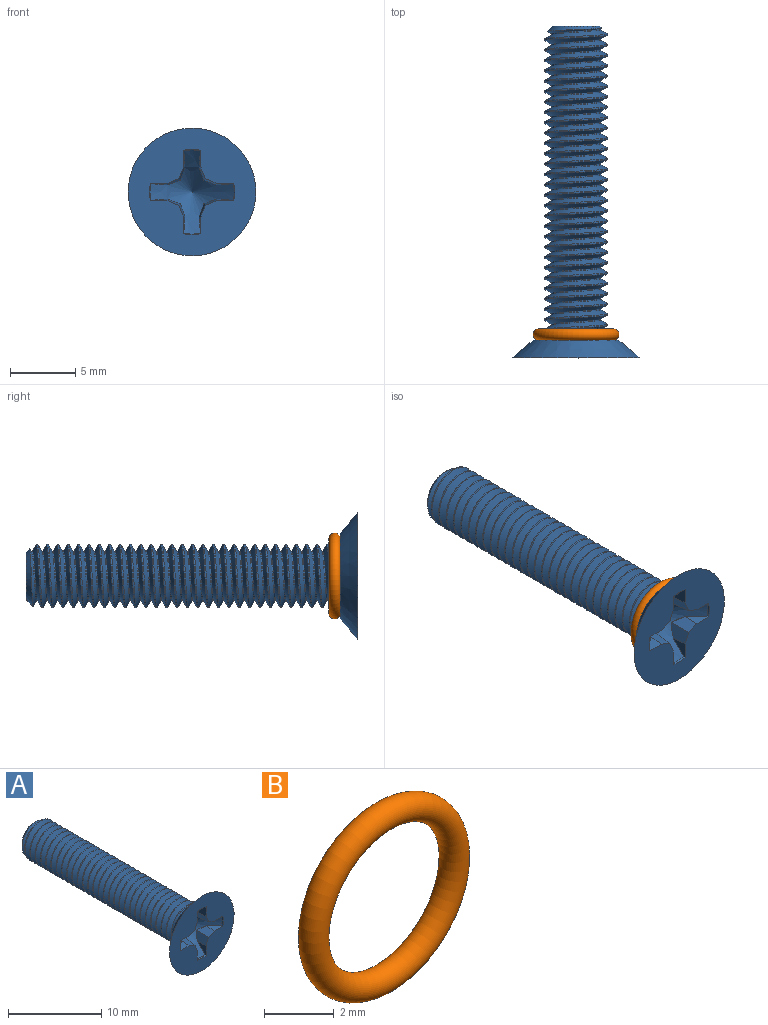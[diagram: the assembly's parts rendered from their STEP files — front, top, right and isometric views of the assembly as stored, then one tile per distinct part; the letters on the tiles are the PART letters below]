
ASSEMBLY  parts=2 mates=1
PART A: 60 faces, bbox 10.1x26x10.1 mm
  f0: cone r=4.27mm half-angle=50deg, axis (0,-1,0), area 20.8mm2, adj f1,f41,f42,f43,f44,f45,f46,f47
  f1: cone r=3.26mm half-angle=15deg, axis (0,-1,0), area 0.2mm2, adj f0,f40,f45,f56
  f2: cone r=4.89mm half-angle=50deg, axis (0,-1,0), area 53.8mm2, adj f39,f40
  f3: cylinder r=1.88mm len=23.12mm, axis (0,-1,0), area 34.1mm2, adj f33,f36,f37,f38
  f4: cylinder r=2.41mm len=4.83mm, axis (0,-1,0), area 14.2mm2, adj f5,f36,f37,f38,f39
  f5: cylinder r=2.41mm len=4.83mm, axis (0,-1,0), area 1.5mm2, adj f4,f6,f36,f37
  f6: cylinder r=2.41mm len=4.83mm, axis (0,-1,0), area 1.5mm2, adj f5,f7,f36,f37
  f7: cylinder r=2.41mm len=4.83mm, axis (0,-1,0), area 1.5mm2, adj f6,f8,f36,f37
  f8: cylinder r=2.41mm len=4.83mm, axis (0,-1,0), area 1.5mm2, adj f7,f9,f36,f37
  f9: cylinder r=2.41mm len=4.83mm, axis (0,-1,0), area 1.5mm2, adj f8,f10,f36,f37
  f10: cylinder r=2.41mm len=4.83mm, axis (0,-1,0), area 1.5mm2, adj f9,f11,f36,f37
  f11: cylinder r=2.41mm len=4.83mm, axis (0,-1,0), area 1.5mm2, adj f10,f12,f36,f37
  f12: cylinder r=2.41mm len=4.83mm, axis (0,-1,0), area 1.5mm2, adj f11,f13,f36,f37
  f13: cylinder r=2.41mm len=4.83mm, axis (0,-1,0), area 1.5mm2, adj f12,f14,f36,f37
  f14: cylinder r=2.41mm len=4.83mm, axis (0,-1,0), area 1.5mm2, adj f13,f15,f36,f37
  f15: cylinder r=2.41mm len=4.83mm, axis (0,-1,0), area 1.5mm2, adj f14,f16,f36,f37
  f16: cylinder r=2.41mm len=4.83mm, axis (0,-1,0), area 1.5mm2, adj f15,f17,f36,f37
  f17: cylinder r=2.41mm len=4.83mm, axis (0,-1,0), area 1.5mm2, adj f16,f18,f36,f37
  f18: cylinder r=2.41mm len=4.83mm, axis (0,-1,0), area 1.5mm2, adj f17,f19,f36,f37
  f19: cylinder r=2.41mm len=4.83mm, axis (0,-1,0), area 1.5mm2, adj f18,f20,f36,f37
  f20: cylinder r=2.41mm len=4.83mm, axis (0,-1,0), area 1.5mm2, adj f19,f21,f36,f37
  f21: cylinder r=2.41mm len=4.83mm, axis (0,-1,0), area 1.5mm2, adj f20,f22,f36,f37
  f22: cylinder r=2.41mm len=4.83mm, axis (0,-1,0), area 1.5mm2, adj f21,f23,f36,f37
  f23: cylinder r=2.41mm len=4.83mm, axis (0,-1,0), area 1.5mm2, adj f22,f24,f36,f37
  f24: cylinder r=2.41mm len=4.83mm, axis (0,-1,0), area 1.5mm2, adj f23,f25,f36,f37
  f25: cylinder r=2.41mm len=4.83mm, axis (0,-1,0), area 1.5mm2, adj f24,f26,f36,f37
  f26: cylinder r=2.41mm len=4.83mm, axis (0,-1,0), area 1.5mm2, adj f25,f27,f36,f37
  f27: cylinder r=2.41mm len=4.83mm, axis (0,-1,0), area 1.5mm2, adj f26,f28,f36,f37
  f28: cylinder r=2.41mm len=4.83mm, axis (0,-1,0), area 1.5mm2, adj f27,f29,f36,f37
  f29: cylinder r=2.41mm len=4.83mm, axis (0,-1,0), area 1.5mm2, adj f28,f30,f36,f37
  f30: cylinder r=2.41mm len=4.83mm, axis (0,-1,0), area 1.5mm2, adj f29,f31,f36,f37
  f31: cylinder r=2.41mm len=4.83mm, axis (0,-1,0), area 1.5mm2, adj f30,f32,f36,f37
  f32: cylinder r=2.41mm len=4.83mm, axis (0,-1,0), area 1.2mm2, adj f31,f34,f36,f37
  f33: cone r=2.41mm half-angle=45deg, axis (0,-1,0), area 4.9mm2, adj f3,f34,f35,f36,f37
  f34: cone r=2.41mm half-angle=45deg, axis (0,-1,0), area 1mm2, adj f32,f33,f36,f37
  f35: plane 3.64x3.64mm, normal (0,1,0), area 10.4mm2, adj f33
  f36: bspline ~23.52x4.83mm, area 238.4mm2, adj f3,f4,f5,f6,f7,f8,f9,f10
  f37: bspline ~23.72x4.8mm, area 238.4mm2, adj f3,f4,f5,f6,f7,f8,f9,f10
  f38: plane 5.15x5.15mm, normal (0,1,0), area 3.7mm2, adj f3,f4,f36,f37
  f39: plane 6.57x6.57mm, normal (0,1,0), area 15.6mm2, adj f2,f4
  f40: plane 9.78x9.78mm, normal (0,-1,0), area 58mm2, adj f1,f2,f41,f42,f43,f44,f45,f46
  f41: cone r=3.26mm half-angle=15deg, axis (0,-1,0), area 0.2mm2, adj f0,f40,f42,f50
  f42: plane 1.49x1.39mm, normal (-1,-0.09,0), area 0.8mm2, adj f0,f40,f41,f43
  f43: plane 2.01x1.25mm, normal (-0.92,-0.09,-0.38), area 1.5mm2, adj f0,f40,f42,f44
  f44: plane 2.01x1.25mm, normal (-0.38,-0.09,-0.92), area 1.5mm2, adj f0,f40,f43,f45
  f45: plane 1.49x1.39mm, normal (0,-0.09,-1), area 0.8mm2, adj f0,f1,f40,f44
  f46: cone r=3.26mm half-angle=15deg, axis (0,-1,0), area 0.2mm2, adj f0,f40,f47,f55
  f47: plane 1.49x1.39mm, normal (0,-0.09,-1), area 0.8mm2, adj f0,f40,f46,f48
  f48: plane 2.01x1.25mm, normal (0.38,-0.09,-0.92), area 1.5mm2, adj f0,f40,f47,f49
  f49: plane 2.01x1.25mm, normal (0.92,-0.09,-0.38), area 1.5mm2, adj f0,f40,f48,f50
  f50: plane 1.49x1.39mm, normal (1,-0.09,0), area 0.8mm2, adj f0,f40,f41,f49
  f51: cone r=3.26mm half-angle=15deg, axis (0,-1,0), area 0.2mm2, adj f0,f40,f52,f59
  f52: plane 1.49x1.39mm, normal (1,-0.09,0), area 0.8mm2, adj f0,f40,f51,f53
  f53: plane 2.01x1.25mm, normal (0.92,-0.09,0.38), area 1.5mm2, adj f0,f40,f52,f54
  f54: plane 2.01x1.25mm, normal (0.38,-0.09,0.92), area 1.5mm2, adj f0,f40,f53,f55
  f55: plane 1.49x1.39mm, normal (0,-0.09,1), area 0.8mm2, adj f0,f40,f46,f54
  f56: plane 1.49x1.39mm, normal (0,-0.09,1), area 0.8mm2, adj f0,f1,f40,f57
  f57: plane 2.01x1.25mm, normal (-0.38,-0.09,0.92), area 1.5mm2, adj f0,f40,f56,f58
  f58: plane 2.01x1.25mm, normal (-0.92,-0.09,0.38), area 1.5mm2, adj f0,f40,f57,f59
  f59: plane 1.49x1.39mm, normal (-1,-0.09,0), area 0.8mm2, adj f0,f40,f51,f58
PART B: 1 faces, bbox 7.1x0.9x7.1 mm
  f0: torus R=2.85mm, axis (0,-1,0), area 49mm2
PLACE A t=(-3.47,-9.54,3.1)mm
PLACE B t=(-3.47,-9.54,3.1)mm
MATE slider A.f0 <-> B.f0  axis (0,1,0) through (-3.47,-9.54,3.1)mm
